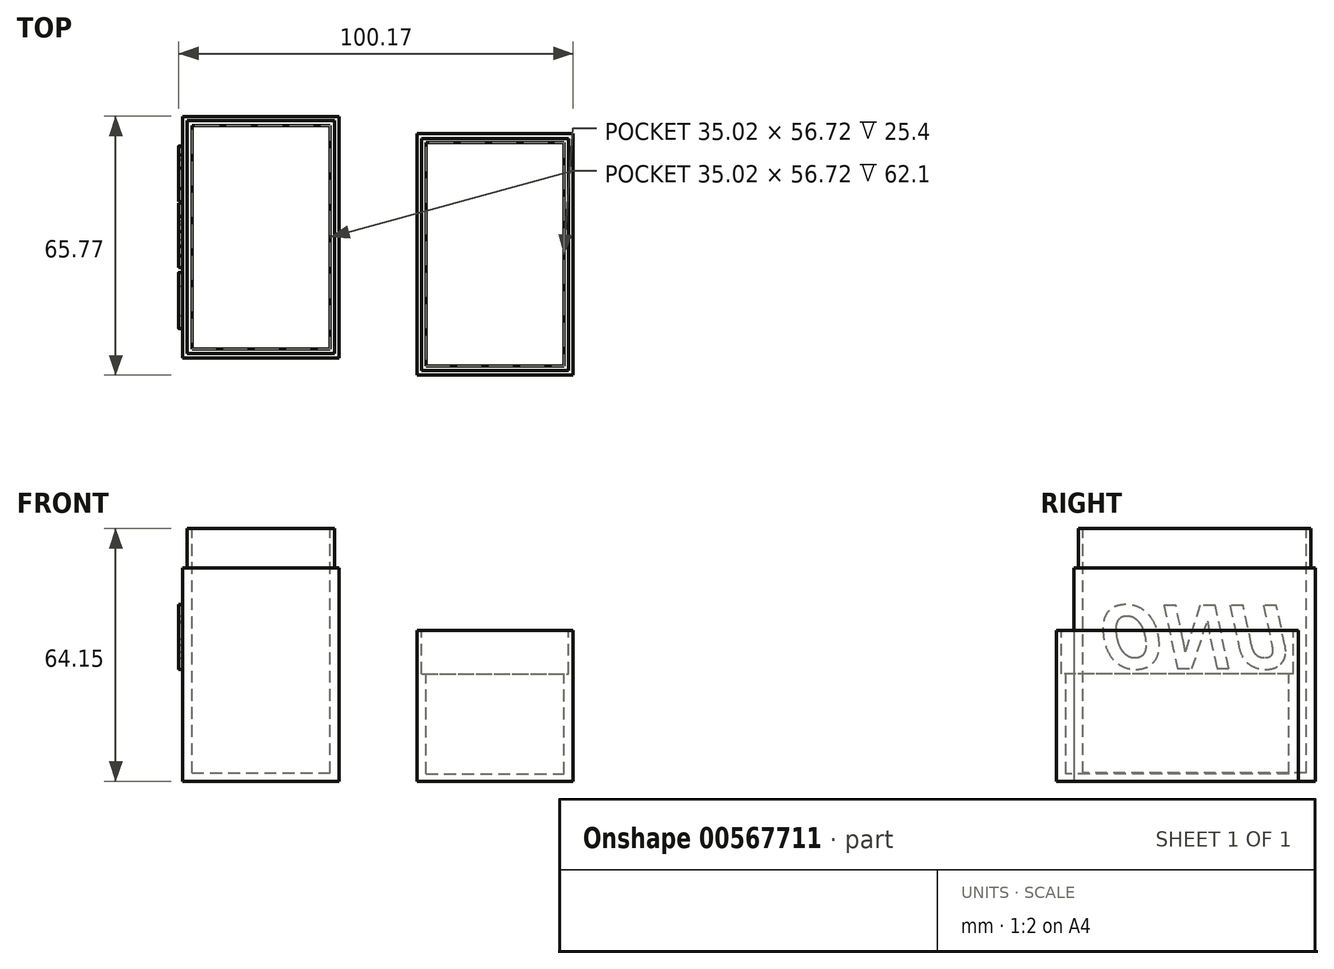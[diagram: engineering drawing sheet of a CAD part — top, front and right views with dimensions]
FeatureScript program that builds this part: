
annotation { "Feature Type Name" : "Feature", "Feature Type Description" : "" }
export const myFeature = defineFeature(function(context is Context, id is Id, definition is map)
    precondition{}
    {
        {
            var Q0;
            Q0=qCreatedBy(makeId("Top.planeOp"),FACE);
            var sketch = newSketch(context, id + "F0", { "sketchPlane" : qUnion([Q0])});
            skLineSegment(sketch, "E0.bottom", {"start": v(-52.87, 34.78) * mm, "end": v(-13.17, 34.78) * mm});
            skLineSegment(sketch, "E0.top", {"start": v(-52.87, -26.62) * mm, "end": v(-13.17, -26.62) * mm});
            skLineSegment(sketch, "E0.left", {"start": v(-52.87, 34.78) * mm, "end": v(-52.87, -26.62) * mm});
            skLineSegment(sketch, "E0.right", {"start": v(-13.17, 34.78) * mm, "end": v(-13.17, -26.62) * mm});
            skSolve(sketch);
        }
        {
            var Q0;
            Q0 = qSketchRegion(id + "F0", true);
            extrude(context, id + "F1", {"entities" : qUnion([Q0]), "depth" : 54.15 * mm, "offsetDistance" : 25 * mm});
        }
        {
            var Q0;
            Q0=makeQuery(id+"F1.opExtrude","CAP_FACE",FACE,{"disambiguationData":[OSD([sQuery(id+"F0.wireOp",EDGE,"E0.bottom"),sQuery(id+"F0.wireOp",EDGE,"E0.top"),sQuery(id+"F0.wireOp",EDGE,"E0.left"),sQuery(id+"F0.wireOp",EDGE,"E0.right")])],"isStart":false});
            var sketch = newSketch(context, id + "F2", { "sketchPlane" : qUnion([Q0])});
            skLineSegment(sketch, "E1.bottom", {"start": v(-14.3, 33.64) * mm, "end": v(-51.73, 33.64) * mm});
            skLineSegment(sketch, "E1.top", {"start": v(-14.3, -25.48) * mm, "end": v(-51.73, -25.48) * mm});
            skLineSegment(sketch, "E1.left", {"start": v(-14.3, 33.64) * mm, "end": v(-14.3, -25.48) * mm});
            skLineSegment(sketch, "E1.right", {"start": v(-51.73, 33.64) * mm, "end": v(-51.73, -25.48) * mm});
            skSolve(sketch);
        }
        {
            var Q0;
            Q0 = qSketchRegion(id + "F2", true);
            extrude(context, id + "F3", {"entities" : qUnion([Q0]), "operationType" : NewBodyOperationType.ADD, "depth" : 10 * mm, "offsetDistance" : 25 * mm});
        }
        {
            var Q0;
            Q0=makeQuery(id+"F3.opExtrude","CAP_FACE",FACE,{"disambiguationData":[OSD([sQuery(id+"F2.wireOp",EDGE,"E1.bottom"),sQuery(id+"F2.wireOp",EDGE,"E1.top"),sQuery(id+"F2.wireOp",EDGE,"E1.left"),sQuery(id+"F2.wireOp",EDGE,"E1.right")])],"isStart":false});
            var sketch = newSketch(context, id + "F4", { "sketchPlane" : qUnion([Q0])});
            skLineSegment(sketch, "E2.bottom", {"start": v(-50.53, 32.44) * mm, "end": v(-15.5, 32.44) * mm});
            skLineSegment(sketch, "E2.top", {"start": v(-50.53, -24.28) * mm, "end": v(-15.5, -24.28) * mm});
            skLineSegment(sketch, "E2.left", {"start": v(-50.53, 32.44) * mm, "end": v(-50.53, -24.28) * mm});
            skLineSegment(sketch, "E2.right", {"start": v(-15.5, 32.44) * mm, "end": v(-15.5, -24.28) * mm});
            skSolve(sketch);
        }
        {
            var Q0;
            Q0 = qSketchRegion(id + "F4", true);
            extrude(context, id + "F5", {"entities" : qUnion([Q0]), "operationType" : NewBodyOperationType.REMOVE, "oppositeDirection" : true, "depth" : 62.1 * mm, "offsetDistance" : 25 * mm});
        }
        {
            var Q0;
            Q0=qCreatedBy(makeId("Top.planeOp"),FACE);
            var sketch = newSketch(context, id + "F6", { "sketchPlane" : qUnion([Q0])});
            skLineSegment(sketch, "E3.bottom", {"start": v(6.6, 30.4) * mm, "end": v(46.3, 30.4) * mm});
            skLineSegment(sketch, "E3.top", {"start": v(6.6, -31) * mm, "end": v(46.3, -31) * mm});
            skLineSegment(sketch, "E3.left", {"start": v(6.6, 30.4) * mm, "end": v(6.6, -31) * mm});
            skLineSegment(sketch, "E3.right", {"start": v(46.3, 30.4) * mm, "end": v(46.3, -31) * mm});
            skSolve(sketch);
        }
        {
            var Q0;
            Q0 = qSketchRegion(id + "F6", true);
            extrude(context, id + "F7", {"entities" : qUnion([Q0]), "depth" : ((26.2 + 2.1) + 10) * mm, "offsetDistance" : 25 * mm});
        }
        {
            var Q0;
            Q0=makeQuery(id+"F7.opExtrude","CAP_FACE",FACE,{"disambiguationData":[OSD([sQuery(id+"F6.wireOp",EDGE,"E3.bottom"),sQuery(id+"F6.wireOp",EDGE,"E3.top"),sQuery(id+"F6.wireOp",EDGE,"E3.left"),sQuery(id+"F6.wireOp",EDGE,"E3.right")])],"isStart":false});
            var sketch = newSketch(context, id + "F8", { "sketchPlane" : qUnion([Q0])});
            skLineSegment(sketch, "E4.bottom", {"start": v(7.82, 29.19) * mm, "end": v(45.08, 29.19) * mm});
            skLineSegment(sketch, "E4.top", {"start": v(7.82, -29.77) * mm, "end": v(45.08, -29.77) * mm});
            skLineSegment(sketch, "E4.left", {"start": v(7.82, 29.19) * mm, "end": v(7.82, -29.77) * mm});
            skLineSegment(sketch, "E4.right", {"start": v(45.08, 29.19) * mm, "end": v(45.08, -29.77) * mm});
            skSolve(sketch);
        }
        {
            var Q0;
            Q0 = qSketchRegion(id + "F8", true);
            extrude(context, id + "F9", {"entities" : qUnion([Q0]), "operationType" : NewBodyOperationType.REMOVE, "oppositeDirection" : true, "depth" : 11 * mm, "offsetDistance" : 25 * mm});
        }
        {
            var Q0;
            Q0=makeQuery(id+"F9.boolean.opBoolean","COPY",FACE,{"derivedFrom":makeQuery(id+"F9.opExtrude","CAP_FACE",FACE,{"disambiguationData":[OSD([sQuery(id+"F8.wireOp",EDGE,"E4.bottom"),sQuery(id+"F8.wireOp",EDGE,"E4.top"),sQuery(id+"F8.wireOp",EDGE,"E4.left"),sQuery(id+"F8.wireOp",EDGE,"E4.right")])],"isStart":false})});
            var sketch = newSketch(context, id + "F10", { "sketchPlane" : qUnion([Q0])});
            skLineSegment(sketch, "E5.bottom", {"start": v(8.94, 28.07) * mm, "end": v(43.96, 28.07) * mm});
            skLineSegment(sketch, "E5.top", {"start": v(8.94, -28.65) * mm, "end": v(43.96, -28.65) * mm});
            skLineSegment(sketch, "E5.left", {"start": v(8.94, 28.07) * mm, "end": v(8.94, -28.65) * mm});
            skLineSegment(sketch, "E5.right", {"start": v(43.96, 28.07) * mm, "end": v(43.96, -28.65) * mm});
            skSolve(sketch);
        }
        {
            var Q0;
            Q0 = qSketchRegion(id + "F10", true);
            extrude(context, id + "F11", {"entities" : qUnion([Q0]), "operationType" : NewBodyOperationType.REMOVE, "oppositeDirection" : true, "depth" : 25.4 * mm, "offsetDistance" : 25 * mm});
        }
        {
            var Q0;
            Q0=qCreatedBy(makeId("Top.planeOp"),FACE);
            var sketch = newSketch(context, id + "F12", { "sketchPlane" : qUnion([Q0])});
            skLineSegment(sketch, "E6.bottom", {"start": v(-40.01, 95.17) * mm, "end": v(-4.71, 95.17) * mm});
            skLineSegment(sketch, "E6.top", {"start": v(-40.01, 39.12) * mm, "end": v(-4.71, 39.12) * mm});
            skLineSegment(sketch, "E6.left", {"start": v(-40.01, 95.17) * mm, "end": v(-40.01, 39.12) * mm});
            skLineSegment(sketch, "E6.right", {"start": v(-4.71, 95.17) * mm, "end": v(-4.71, 39.12) * mm});
            skSolve(sketch);
        }
        {
            var Q0;
            Q0 = qSketchRegion(id + "F12", true);
            extrude(context, id + "F13", {"entities" : qUnion([Q0]), "depth" : 87.1 * mm, "offsetDistance" : 25 * mm});
        }
        {
            var Q0;
            Q0=makeQuery(id+"F13.opExtrude","SWEPT_BODY",BODY,{"disambiguationData":[OSD([sQuery(id+"F12.wireOp",EDGE,"E6.bottom"),sQuery(id+"F12.wireOp",EDGE,"E6.top"),sQuery(id+"F12.wireOp",EDGE,"E6.left"),sQuery(id+"F12.wireOp",EDGE,"E6.right")])]});
            deleteBodies(context, id + "F14", {"entities" : qUnion([Q0])});
        }
        {
            var Q0;
            Q0=makeQuery(id+"F1.opExtrude","SWEPT_FACE",FACE,{"disambiguationData":[OSD([sQuery(id+"F0.wireOp",EDGE,"E0.left")])]});
            var sketch = newSketch(context, id + "F15", { "sketchPlane" : qUnion([Q0])});
            skText(sketch, "E7", { "text": "UNO", "fontName": "OpenSans-BoldItalic.ttf"});
            const initialGuessF15  = {"E7": [-0.02878, 0.02864, 1, 0, 0.0161]};
            skSetInitialGuess(sketch, initialGuessF15);
            skSolve(sketch);
        }
        {
            var Q0;
            Q0 = qSketchRegion(id + "F15", true);
            extrude(context, id + "F16", {"entities" : qUnion([Q0]), "operationType" : NewBodyOperationType.ADD, "depth" : 1 * mm, "offsetDistance" : 25 * mm});
        }
    });
